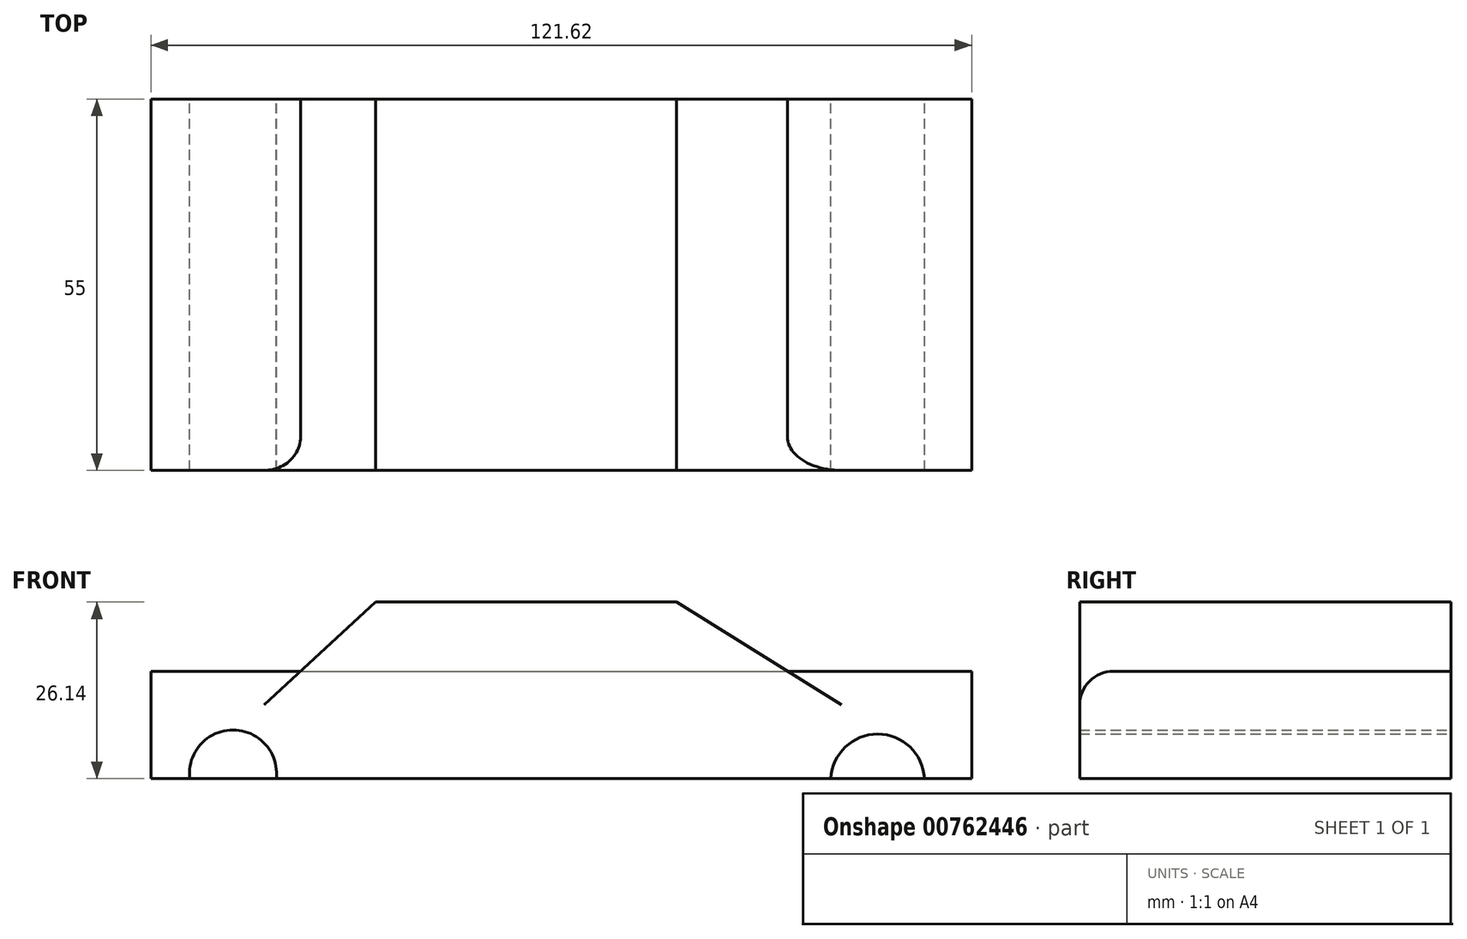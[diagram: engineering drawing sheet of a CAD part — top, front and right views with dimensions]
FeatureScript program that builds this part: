
annotation { "Feature Type Name" : "Feature", "Feature Type Description" : "" }
export const myFeature = defineFeature(function(context is Context, id is Id, definition is map)
    precondition{}
    {
        {
            var Q0;
            Q0=qCreatedBy(makeId("Front.planeOp"),FACE);
            var sketch = newSketch(context, id + "F0", { "sketchPlane" : qUnion([Q0])});
            skLineSegment(sketch, "E0.bottom", {"start": v(-56, 0) * mm, "end": v(65.6, 0) * mm});
            skLineSegment(sketch, "E0.top", {"start": v(-56, 15.9) * mm, "end": v(65.6, 15.9) * mm});
            skLineSegment(sketch, "E0.left", {"start": v(-56, 0) * mm, "end": v(-56, 15.9) * mm});
            skLineSegment(sketch, "E0.right", {"start": v(65.6, 0) * mm, "end": v(65.6, 15.9) * mm});
            skLineSegment(sketch, "E1.bottom", {"start": v(-29.34, 15.9) * mm, "end": v(33.4, 15.9) * mm});
            skLineSegment(sketch, "E1.top", {"start": v(-22.72, 26.14) * mm, "end": v(21.87, 26.14) * mm});
            skLineSegment(sketch, "E2", {"start": v(21.87, 26.14) * mm, "end": v(38.3, 15.9) * mm});
            skLineSegment(sketch, "E3", {"start": v(-22.72, 26.14) * mm, "end": v(-33.82, 15.9) * mm});
            skSolve(sketch);
        }
        {
            var Q0;
            Q0=makeQuery(id+"F0.imprint","IMPRINT",FACE,{"disambiguationData":[TD([[makeQuery(id+"F0.imprint","IMPRINT",EDGE,{"derivedFrom":sQuery(id+"F0.wireOp",EDGE,"E0.bottom")}),1.0]])]});
            var sketch = newSketch(context, id + "F1", { "sketchPlane" : qUnion([Q0])});
            skArc(sketch, "E4", {"start": v(58.6, 0) * mm, "mid": v(51.67, 6.58) * mm, "end": v(44.74, 0) * mm});
            skArc(sketch, "E5", {"start": v(-37.42, 0) * mm, "mid": v(-43.83, 7.2) * mm, "end": v(-50.24, 0) * mm});
            skSolve(sketch);
        }
        {
            var Q0;
            {var subQ9=sQuery(id+"F1.wireOp",EDGE,"E4");Q0=makeQuery(id+"F1.imprint","IMPRINT",FACE,{"disambiguationData":[TD([[makeQuery(id+"F1.imprint","IMPRINT",EDGE,{"derivedFrom":subQ9}),-1.0]])]});}
            var Q1;
            Q1=makeQuery(id+"F0.imprint","IMPRINT",FACE,{"disambiguationData":[TD([[makeQuery(id+"F0.imprint","IMPRINT",EDGE,{"derivedFrom":sQuery(id+"F0.wireOp",EDGE,"E0.bottom")}),1.0]])]});
            var Q2;
            Q2=makeQuery(id+"F0.imprint","IMPRINT",FACE,{"disambiguationData":[TD([[makeQuery(id+"F0.imprint","IMPRINT",EDGE,{"derivedFrom":sQuery(id+"F0.wireOp",EDGE,"E1.top")}),-1.0]])]});
            extrude(context, id + "F2", {"entities" : qUnion([Q0, Q1, Q2]), "depth" : 55 * mm, "offsetDistance" : 25 * mm});
        }
        {
            var Q0;
            {var subQ0=sQuery(id+"F0.wireOp",EDGE,"E0.top");Q0=makeQuery(id+"F2.opExtrude","CAP_EDGE",EDGE,{"disambiguationData":[OSD([subQ0]),TDD([makeQuery(id+"F0.imprint","IMPRINT",EDGE,{"disambiguationData":[TD([[makeQuery(id+"F0.imprint","INTERSECT",VERTEX,{"derivedFrom":[subQ0,sQuery(id+"F0.wireOp",EDGE,"E0.right")]}),1.0]])],"derivedFrom":subQ0})])],"isStart":false});}
            fillet(context, id + "F3", {"entities" : qUnion([Q0]), "radius" : 5 * mm, "tangentPropagation" : true, "allowEdgeOverflow" : false});
        }
        {
            var Q0;
            {var subQ0=sQuery(id+"F0.wireOp",EDGE,"E0.top");var subQ1=makeQuery(id+"F0.imprint","IMPRINT",VERTEX,{"disambiguationData":[OD(0.0)],"derivedFrom":subQ0});var subQ4=makeQuery(id+"F0.imprint","IMPRINT",VERTEX,{"disambiguationData":[OD(1.0)],"derivedFrom":subQ0});Q0=makeQuery(id+"F2.opExtrude","CAP_EDGE",EDGE,{"disambiguationData":[OSD([subQ0]),TDD([makeQuery(id+"F1.imprint","IMPRINT",EDGE,{"derivedFrom":makeQuery(id+"F0.imprint","IMPRINT",EDGE,{"disambiguationData":[TD([[subQ1,-1.0]])],"derivedFrom":subQ0})}),makeQuery(id+"F1.imprint","IMPRINT",EDGE,{"derivedFrom":makeQuery(id+"F0.imprint","IMPRINT",EDGE,{"disambiguationData":[TD([[makeQuery(id+"F0.imprint","INTERSECT",VERTEX,{"derivedFrom":[subQ0,sQuery(id+"F0.wireOp",EDGE,"E0.right")]}),1.0]])],"derivedFrom":subQ0})}),makeQuery(id+"F1.imprint","IMPRINT",EDGE,{"derivedFrom":makeQuery(id+"F0.imprint","IMPRINT",EDGE,{"disambiguationData":[TD([[makeQuery(id+"F0.imprint","INTERSECT",VERTEX,{"derivedFrom":[subQ0,sQuery(id+"F0.wireOp",EDGE,"E0.left")]}),-1.0]])],"derivedFrom":subQ0})}),makeQuery(id+"F1.imprint","IMPRINT",EDGE,{"derivedFrom":makeQuery(id+"F0.imprint","IMPRINT",EDGE,{"disambiguationData":[TD([[subQ4,-1.0]])],"derivedFrom":subQ0})}),makeQuery(id+"F1.imprint","IMPRINT",EDGE,{"derivedFrom":makeQuery(id+"F0.imprint","IMPRINT",EDGE,{"disambiguationData":[TD([[subQ1,1.0]])],"derivedFrom":subQ0})})])],"isStart":false});}
            fillet(context, id + "F4", {"entities" : qUnion([Q0]), "radius" : 5 * mm, "tangentPropagation" : true, "allowEdgeOverflow" : false});
        }
        {
            var Q0;
            {var subQ0=sQuery(id+"F0.wireOp",EDGE,"E0.top");Q0=makeQuery(id+"F2.opExtrude","CAP_EDGE",EDGE,{"disambiguationData":[OSD([subQ0]),TDD([makeQuery(id+"F0.imprint","IMPRINT",EDGE,{"disambiguationData":[TD([[makeQuery(id+"F0.imprint","INTERSECT",VERTEX,{"derivedFrom":[subQ0,sQuery(id+"F0.wireOp",EDGE,"E0.left")]}),-1.0]])],"derivedFrom":subQ0})])],"isStart":false});}
            fillet(context, id + "F5", {"entities" : qUnion([Q0]), "radius" : 5 * mm, "tangentPropagation" : true, "allowEdgeOverflow" : false});
        }
    });
